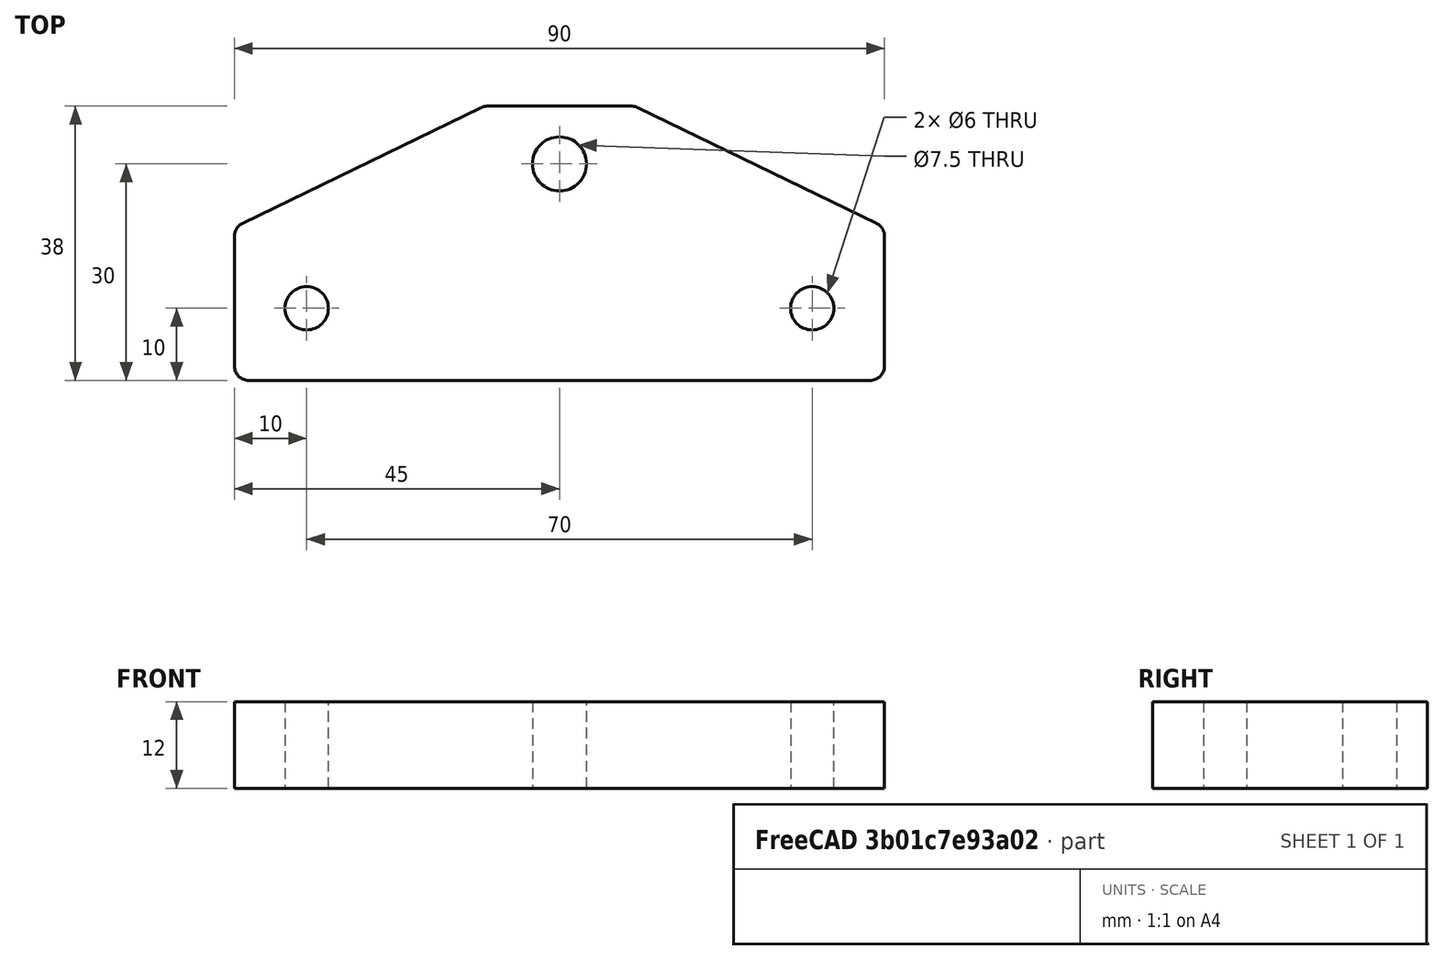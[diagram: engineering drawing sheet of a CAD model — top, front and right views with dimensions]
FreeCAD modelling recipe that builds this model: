
FCSTD DOCUMENT  (FreeCAD 0.19R24366 (Git))
Label: Camera mount plate 12mm
License: All rights reserved
LicenseURL: http://en.wikipedia.org/wiki/All_rights_reserved
objects: Sketcher::SketchObject×1, PartDesign::Pad×1, PartDesign::Body×1
note: 4 computed .brp shape members not serialized (recipe doc carries the construction recipe); baked Part::Feature solids carry a one-line shape summary decoded from their .brp

FEATURE [Sketcher::SketchObject] Sketch
  FullyConstrained = true
  MapMode = 5
  Support = -> [XY_Plane]
  sketch-geometry (23):
    g0: Circle CenterX=-35 CenterY=0 CenterZ=0 NormalX=0 NormalY=0 NormalZ=1 AngleXU=0 Radius=3
    g1: Circle CenterX=35 CenterY=0 CenterZ=0 NormalX=0 NormalY=0 NormalZ=1 AngleXU=0 Radius=3
    g2: Circle CenterX=0 CenterY=20 CenterZ=0 NormalX=0 NormalY=0 NormalZ=1 AngleXU=0 Radius=3.75
    g3: LineSegment StartX=-43 StartY=-10 StartZ=0 EndX=43 EndY=-10 EndZ=0
    g4: LineSegment StartX=45 StartY=-8 StartZ=0 EndX=45 EndY=10 EndZ=0
    g5: LineSegment StartX=-45 StartY=-8 StartZ=0 EndX=-45 EndY=10 EndZ=0
    g6: LineSegment StartX=-43.8725 StartY=11.7996 StartZ=0 EndX=-10.8725 EndY=27.7996 EndZ=0
    g7: LineSegment StartX=10.8725 StartY=27.7996 StartZ=0 EndX=43.8725 EndY=11.7996 EndZ=0
    g8: ArcOfCircle CenterX=-43 CenterY=10 CenterZ=0 NormalX=0 NormalY=0 NormalZ=1 AngleXU=0 Radius=2 StartAngle=2.02225 EndAngle=3.14159
    g9: ArcOfCircle CenterX=-43 CenterY=-8 CenterZ=0 NormalX=0 NormalY=0 NormalZ=1 AngleXU=0 Radius=2 StartAngle=3.14159 EndAngle=4.71239
    g10: ArcOfCircle CenterX=43 CenterY=-8 CenterZ=0 NormalX=0 NormalY=0 NormalZ=1 AngleXU=0 Radius=2 StartAngle=4.71239 EndAngle=6.28319
    g11: ArcOfCircle CenterX=43 CenterY=10 CenterZ=0 NormalX=0 NormalY=0 NormalZ=1 AngleXU=0 Radius=2 StartAngle=0 EndAngle=1.11934
    g12: LineSegment StartX=-45 StartY=10 StartZ=0 EndX=45 EndY=10 EndZ=0
    g13: GeomPoint X=0 Y=10 Z=0
    g14: GeomPoint X=0 Y=-10 Z=0
    g15: LineSegment StartX=-10 StartY=28 StartZ=0 EndX=10 EndY=28 EndZ=0
    g16: ArcOfCircle CenterX=-10 CenterY=26 CenterZ=0 NormalX=0 NormalY=0 NormalZ=1 AngleXU=0 Radius=2 StartAngle=1.5708 EndAngle=2.02225
    g17: ArcOfCircle CenterX=10 CenterY=26 CenterZ=0 NormalX=0 NormalY=0 NormalZ=1 AngleXU=0 Radius=2 StartAngle=1.11934 EndAngle=1.5708
    g18: Circle CenterX=35 CenterY=0 CenterZ=0 NormalX=0 NormalY=0 NormalZ=1 AngleXU=0 Radius=13
    g19: Circle CenterX=-35 CenterY=0 CenterZ=0 NormalX=0 NormalY=0 NormalZ=1 AngleXU=0 Radius=13
    g20: Circle CenterX=0 CenterY=20 CenterZ=0 NormalX=0 NormalY=0 NormalZ=1 AngleXU=0 Radius=6.5
    g21: GeomPoint X=-22 Y=0 Z=0
    g22: GeomPoint X=22 Y=0 Z=0
  constraints (52):
    c: PointOnObject(g0,g-1)
    c: PointOnObject(g2,g-2)
    c: Symmetric(g0,g1,g-2)
    c: DistanceX(g0,g1) = 70
    c: Equal(g0,g1)
    c: Horizontal(g3)
    c: Vertical(g5)
    c: Equal(g4,g5)
    c: Vertical(g4)
    c: Tangent(g6,g8) = 1.5708
    c: Tangent(g5,g8) = 1.5708
    c: Tangent(g3,g9) = -1.5708
    c: Tangent(g5,g9) = 1.5708
    c: Tangent(g4,g10) = -1.5708
    c: Tangent(g3,g10) = -1.5708
    c: Tangent(g4,g11) = -1.5708
    c: Tangent(g7,g11) = 1.5708
    c: Equal(g11,g10)
    c: Equal(g9,g8)
    c: Radius(g9) = 2
    c: Coincident(g12,g5)
    c: Coincident(g12,g4)
    c: PointOnObject(g13,g12)
    c: PointOnObject(g13,g-2)
    c: PointOnObject(g14,g3)
    c: Symmetric(g14,g13,g-1)
    c: DistanceY(g14,g13) = 20
    c: Symmetric(g5,g4,g-2)
    c: DistanceX(g5,g0) = 10
    c: Tangent(g15,g16) = 1.5708
    c: Tangent(g6,g16) = 1.5708
    c: Tangent(g15,g17) = 1.5708
    c: Tangent(g7,g17) = 1.5708
    c: Symmetric(g15,g15,g-2)
    c: Equal(g17,g16)
    c: Equal(g16,g9)
    c: DistanceY(g2,g15) = 8
    c: DistanceX(g15,g15) = 20
    c: DistanceY(g13,g2) = 10
    c: Coincident(g18,g1)
    c: Coincident(g19,g0)
    c: Equal(g19,g18)
    c: Coincident(g20,g2)
    c: Diameter(g20) = 13
    c: Diameter(g19) = 26
    c: PointOnObject(g21,g-1)
    c: PointOnObject(g22,g-1)
    c: PointOnObject(g22,g18)
    c: PointOnObject(g21,g19)
    c: DistanceX(g21,g22) = 44
    c: Diameter(g2) = 7.5
    c: Diameter(g0) = 6
FEATURE [PartDesign::Pad] Pad
  Direction = (1,1,1)
  Length = 12
  Length2 = 100
  Profile = -> Sketch
  Type = 0
FEATURE [PartDesign::Body] Body
  Group = -> [Sketch,Pad]
  Origin = -> Origin
  Tip = -> Pad
